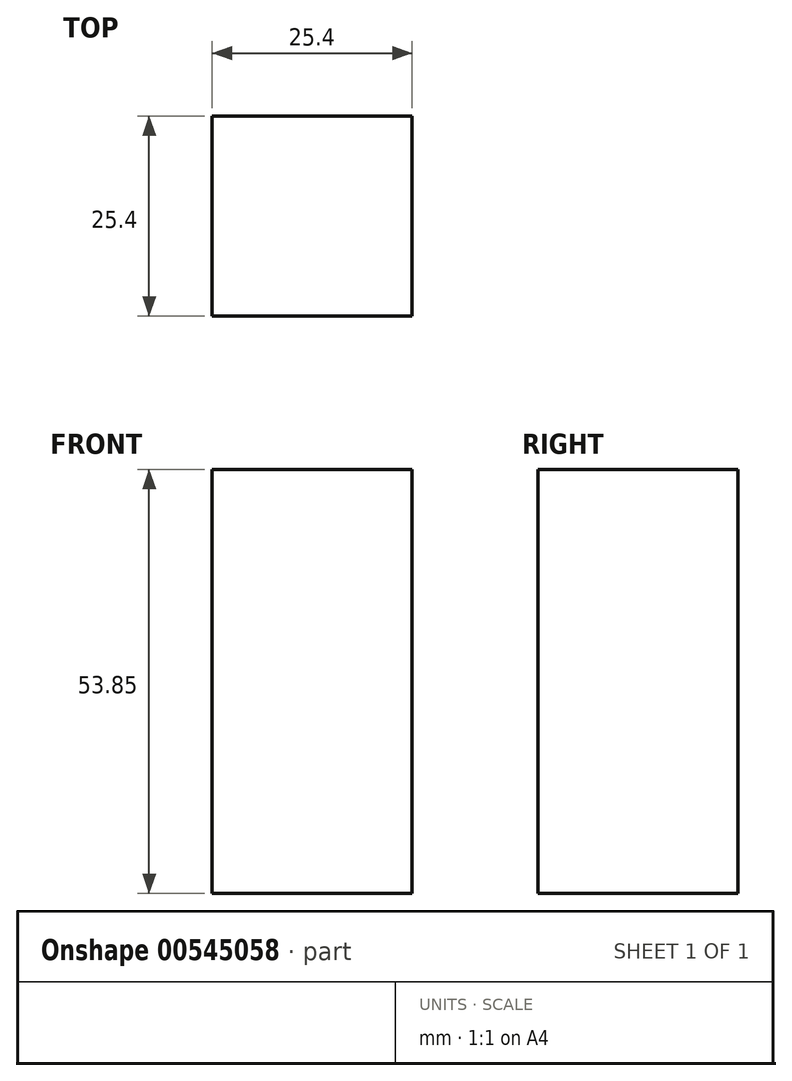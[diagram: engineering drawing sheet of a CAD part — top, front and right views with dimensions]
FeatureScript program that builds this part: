
annotation { "Feature Type Name" : "Feature", "Feature Type Description" : "" }
export const myFeature = defineFeature(function(context is Context, id is Id, definition is map)
    precondition{}
    {
        {
            var Q0;
            Q0=qCreatedBy(makeId("Top.planeOp"),FACE);
            var sketch = newSketch(context, id + "F0", { "sketchPlane" : qUnion([Q0])});
            skLineSegment(sketch, "E0.bottom", {"start": v(12.7, 12.7) * mm, "end": v(-12.7, 12.7) * mm});
            skLineSegment(sketch, "E0.top", {"start": v(12.7, -12.7) * mm, "end": v(-12.7, -12.7) * mm});
            skLineSegment(sketch, "E0.left", {"start": v(12.7, 12.7) * mm, "end": v(12.7, -12.7) * mm});
            skLineSegment(sketch, "E0.right", {"start": v(-12.7, 12.7) * mm, "end": v(-12.7, -12.7) * mm});
            skPoint(sketch, "E0.middle", {"position": v(0, 0) * mm});
            skSolve(sketch);
        }
        {
            var Q0;
            Q0=makeQuery(id+"F0.imprint","IMPRINT",FACE,{"disambiguationData":[TD([[makeQuery(id+"F0.imprint","IMPRINT",EDGE,{"derivedFrom":sQuery(id+"F0.wireOp",EDGE,"E0.bottom")}),1.0]])]});
            extrude(context, id + "F1", {"entities" : qUnion([Q0]), "depth" : 53.85 * mm, "offsetDistance" : 25.4 * mm});
        }
    });
